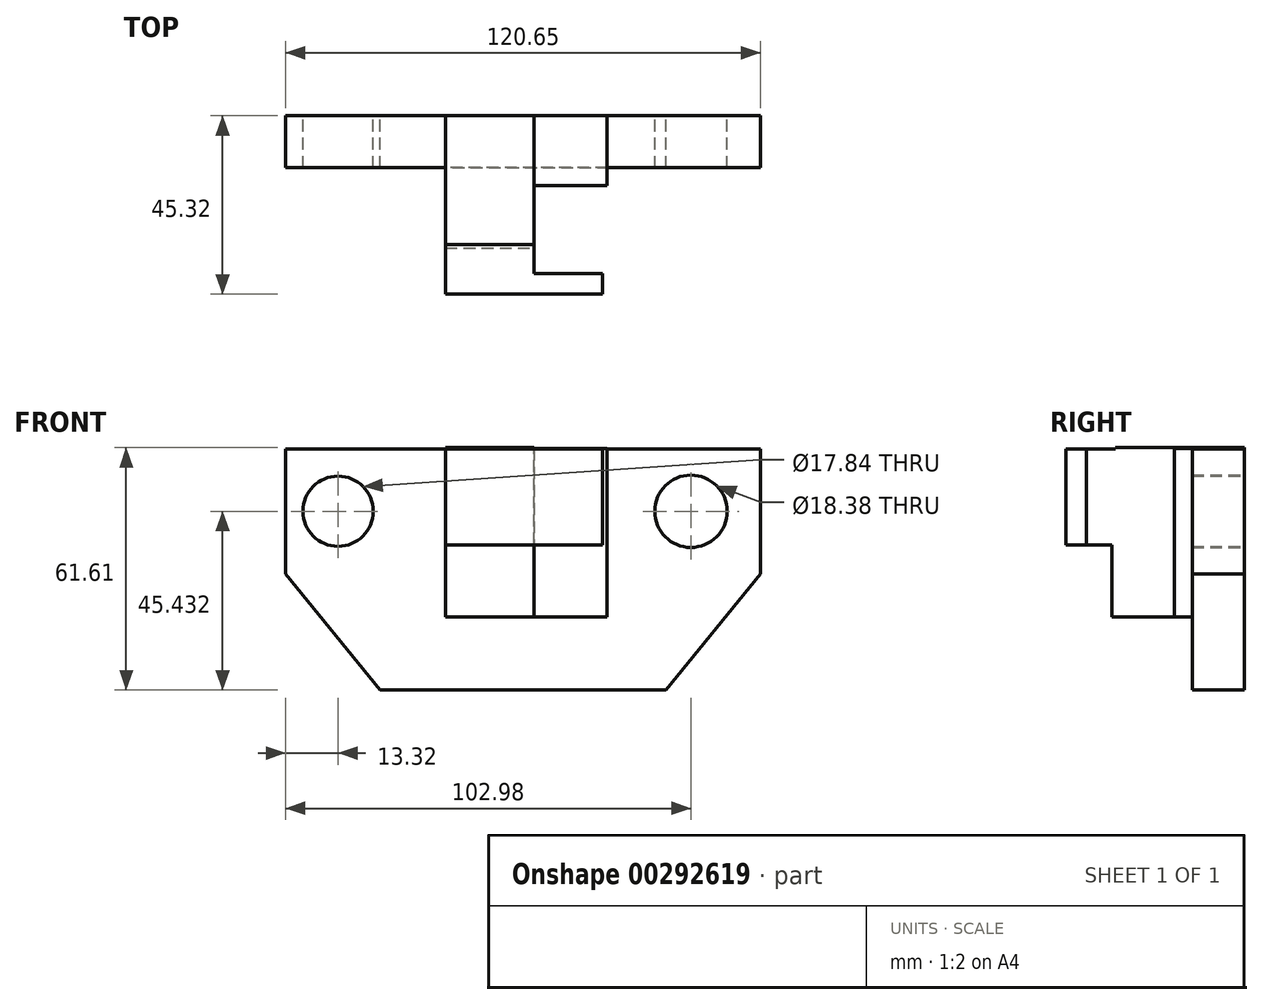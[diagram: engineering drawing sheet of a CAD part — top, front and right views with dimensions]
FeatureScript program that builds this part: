
annotation { "Feature Type Name" : "Feature", "Feature Type Description" : "" }
export const myFeature = defineFeature(function(context is Context, id is Id, definition is map)
    precondition{}
    {
        {
            var Q0;
            Q0=qCreatedBy(makeId("Front.planeOp"),FACE);
            var sketch = newSketch(context, id + "F0", { "sketchPlane" : qUnion([Q0])});
            skLineSegment(sketch, "E0", {"start": v(-63.06, 42.69) * mm, "end": v(-63.06, 10.94) * mm});
            skLineSegment(sketch, "E1", {"start": v(57.59, 10.94) * mm, "end": v(57.59, 42.69) * mm});
            skLineSegment(sketch, "E2", {"start": v(-63.06, 42.69) * mm, "end": v(57.59, 42.69) * mm});
            skLineSegment(sketch, "E3", {"start": v(-63.06, 10.94) * mm, "end": v(-39.02, -18.62) * mm});
            skLineSegment(sketch, "E4", {"start": v(57.59, 10.94) * mm, "end": v(33.55, -18.62) * mm});
            skLineSegment(sketch, "E5", {"start": v(-39.02, -18.62) * mm, "end": v(33.55, -18.62) * mm});
            skCircle(sketch, "E6", {"center": v(-49.74, 26.81) * mm, "radius": 8.92 * mm});
            skPoint(sketch, "E6.centerSnap0", {"position": v(-63.06, 26.81) * mm});
            skCircle(sketch, "E7", {"center": v(39.92, 26.81) * mm, "radius": 9.19 * mm});
            skSolve(sketch);
        }
        {
            var Q0;
            Q0 = qSketchRegion(id + "F0", true);
            extrude(context, id + "F1", {"entities" : qUnion([Q0]), "depth" : 13.2 * mm});
        }
        {
            var Q0;
            Q0=qCreatedBy(makeId("Front.planeOp"),FACE);
            var sketch = newSketch(context, id + "F2", { "sketchPlane" : qUnion([Q0])});
            skLineSegment(sketch, "E8.bottom", {"start": v(-22.44, 42.7) * mm, "end": v(18.65, 42.7) * mm});
            skLineSegment(sketch, "E8.top", {"start": v(-22.44, 0) * mm, "end": v(18.65, 0) * mm});
            skLineSegment(sketch, "E8.left", {"start": v(-22.44, 42.7) * mm, "end": v(-22.44, 0) * mm});
            skLineSegment(sketch, "E8.right", {"start": v(18.65, 42.7) * mm, "end": v(18.65, 0) * mm});
            skSolve(sketch);
        }
        {
            var Q0;
            Q0 = qSketchRegion(id + "F2", true);
            extrude(context, id + "F3", {"entities" : qUnion([Q0]), "operationType" : NewBodyOperationType.ADD, "depth" : 17.78 * mm});
        }
        {
            var Q0;
            Q0=qCreatedBy(makeId("Front.planeOp"),FACE);
            var sketch = newSketch(context, id + "F4", { "sketchPlane" : qUnion([Q0])});
            skLineSegment(sketch, "E9.bottom", {"start": v(-22.44, 43) * mm, "end": v(0, 43) * mm});
            skLineSegment(sketch, "E9.top", {"start": v(-22.44, 0) * mm, "end": v(0, 0) * mm});
            skLineSegment(sketch, "E9.left", {"start": v(-22.44, 43) * mm, "end": v(-22.44, 0) * mm});
            skLineSegment(sketch, "E9.right", {"start": v(0, 43) * mm, "end": v(0, 0) * mm});
            skSolve(sketch);
        }
        {
            var Q0;
            Q0 = qSketchRegion(id + "F4", true);
            extrude(context, id + "F5", {"entities" : qUnion([Q0]), "operationType" : NewBodyOperationType.ADD, "depth" : 32.77 * mm});
        }
        {
            var Q0;
            Q0=qCreatedBy(makeId("Top.planeOp"),FACE);
            var sketch = newSketch(context, id + "F6", { "sketchPlane" : qUnion([Q0])});
            skLineSegment(sketch, "E10", {"start": v(-22.44, -32.5) * mm, "end": v(0, -32.5) * mm});
            skLineSegment(sketch, "E11", {"start": v(0, -32.5) * mm, "end": v(0, -40.08) * mm});
            skLineSegment(sketch, "E12", {"start": v(0, -40.08) * mm, "end": v(17.49, -40.08) * mm});
            skLineSegment(sketch, "E13", {"start": v(17.49, -40.08) * mm, "end": v(17.49, -45.32) * mm});
            skLineSegment(sketch, "E14", {"start": v(17.49, -45.32) * mm, "end": v(-22.44, -45.32) * mm});
            skLineSegment(sketch, "E15", {"start": v(-22.44, -45.32) * mm, "end": v(-22.44, -32.5) * mm});
            skSolve(sketch);
        }
        {
            var Q0;
            Q0 = qSketchRegion(id + "F6", true);
            extrude(context, id + "F7", {"entities" : qUnion([Q0]), "operationType" : NewBodyOperationType.ADD, "depth" : 42.67 * mm});
        }
        {
            var Q0;
            Q0=qCreatedBy(makeId("Top.planeOp"),FACE);
            var sketch = newSketch(context, id + "F8", { "sketchPlane" : qUnion([Q0])});
            skLineSegment(sketch, "E16", {"start": v(-22.44, -33.67) * mm, "end": v(0, -33.67) * mm});
            skLineSegment(sketch, "E17", {"start": v(0, -33.67) * mm, "end": v(0, -40.08) * mm});
            skLineSegment(sketch, "E18", {"start": v(-22.44, -45.32) * mm, "end": v(-22.44, -33.67) * mm});
            skLineSegment(sketch, "E19", {"start": v(0, -40.08) * mm, "end": v(18.07, -40.08) * mm});
            skLineSegment(sketch, "E20", {"start": v(18.07, -40.08) * mm, "end": v(18.07, -45.32) * mm});
            skLineSegment(sketch, "E21", {"start": v(18.07, -45.32) * mm, "end": v(-22.44, -45.32) * mm});
            skSolve(sketch);
        }
        {
            var Q0;
            Q0 = qSketchRegion(id + "F8", true);
            extrude(context, id + "F9", {"entities" : qUnion([Q0]), "operationType" : NewBodyOperationType.REMOVE, "depth" : 18.29 * mm});
        }
    });
